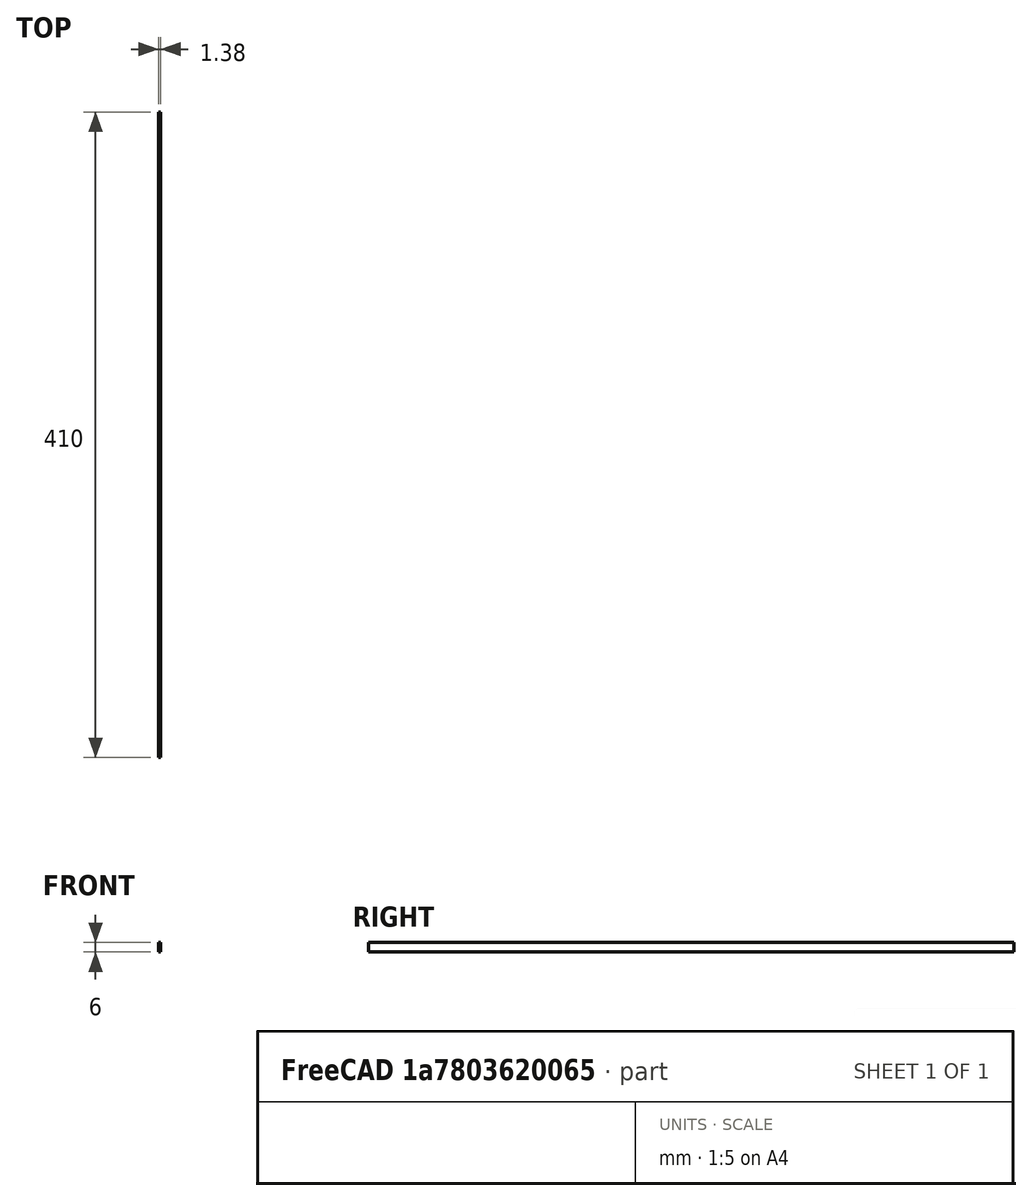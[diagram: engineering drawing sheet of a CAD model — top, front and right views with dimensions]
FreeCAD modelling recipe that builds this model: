
FCSTD DOCUMENT  (FreeCAD 0.20R27078 (Git))
Label: belt 40 mm
License: All rights reserved
LicenseURL: http://en.wikipedia.org/wiki/All_rights_reserved
objects: Sketcher::SketchObject×1, PartDesign::Pad×1, PartDesign::Body×1
note: 4 computed .brp shape members not serialized (recipe doc carries the construction recipe); baked Part::Feature solids carry a one-line shape summary decoded from their .brp

FEATURE [Sketcher::SketchObject] Sketch
  FullyConstrained = true
  MapMode = 5
  Placement = pos=(0,0,0) rot=(1,0,0;1.5708rad)
  Support = -> [XZ_Plane]
  sketch-geometry (4):
    g0: LineSegment StartX=0 StartY=6 StartZ=0 EndX=1.38 EndY=6 EndZ=0
    g1: LineSegment StartX=1.38 StartY=6 StartZ=0 EndX=1.38 EndY=0 EndZ=0
    g2: LineSegment StartX=1.38 StartY=0 StartZ=0 EndX=0 EndY=0 EndZ=0
    g3: LineSegment StartX=0 StartY=0 StartZ=0 EndX=0 EndY=6 EndZ=0
  constraints (12):
    c: Coincident(g0,g1)
    c: Coincident(g1,g2)
    c: Coincident(g2,g3)
    c: Coincident(g3,g0)
    c: Horizontal(g0)
    c: Horizontal(g2)
    c: Vertical(g1)
    c: Vertical(g3)
    c: PointOnObject(g0,g-2)
    c: PointOnObject(g1,g-1)
    c: DistanceY(g3,g3) = 6
    c: DistanceX(g0,g0) = 1.38
FEATURE [PartDesign::Pad] Pad
  Direction = (0,-1,-2e-16)
  Length = 410
  Length2 = 100
  Placement = pos=(0,0,0) rot=(1,0,0;1.5708rad)
  Profile = -> Sketch
  ReferenceAxis = -> Sketch [N_Axis]
  Type = 0
FEATURE [PartDesign::Body] Body  label="belt 410 mm"
  Group = -> [Sketch,Pad]
  Origin = -> Origin
  Tip = -> Pad
